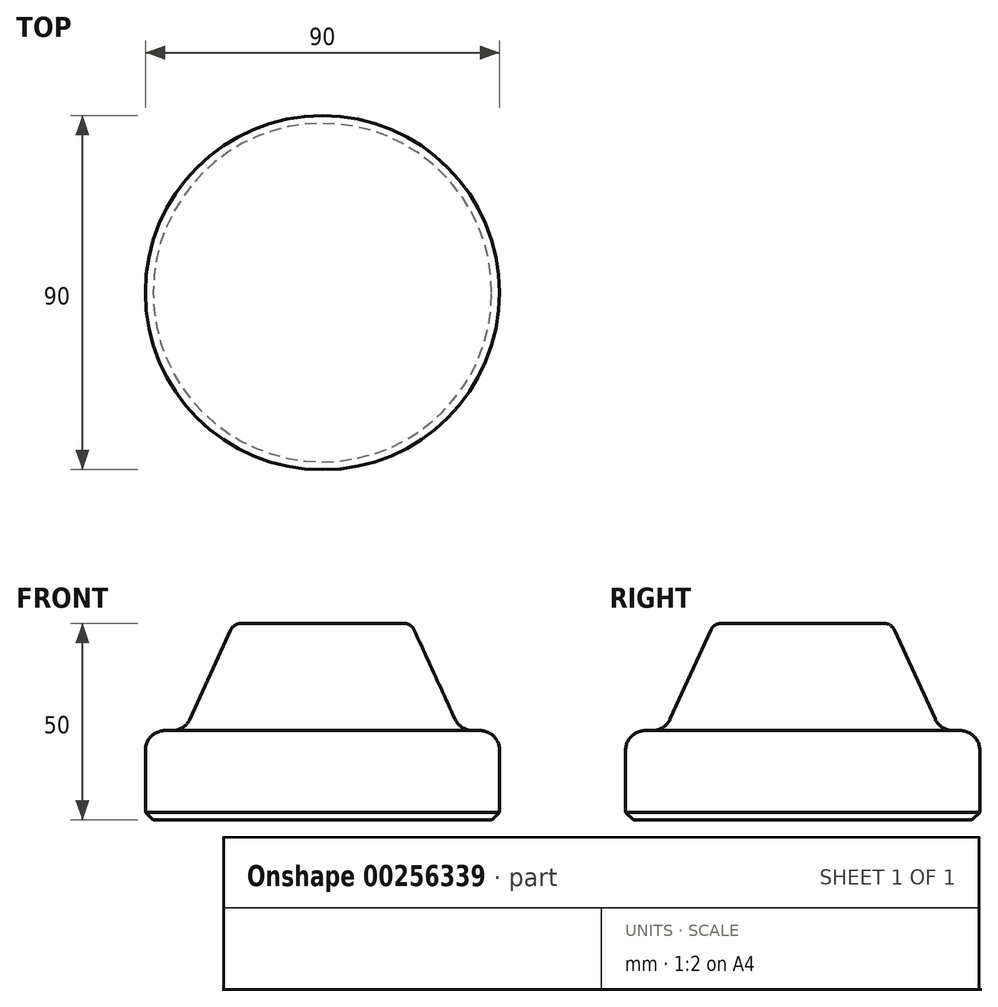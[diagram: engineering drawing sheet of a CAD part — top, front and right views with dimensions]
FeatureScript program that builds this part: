
annotation { "Feature Type Name" : "Feature", "Feature Type Description" : "" }
export const myFeature = defineFeature(function(context is Context, id is Id, definition is map)
    precondition{}
    {
        {
            var Q0;
            Q0=qCreatedBy(makeId("Front.planeOp"),FACE);
            var sketch = newSketch(context, id + "F0", { "sketchPlane" : qUnion([Q0])});
            skLineSegment(sketch, "E0", {"start": v(0, 50) * mm, "end": v(0, 0) * mm});
            skLineSegment(sketch, "E1", {"start": v(0, 0) * mm, "end": v(45, 0) * mm});
            skLineSegment(sketch, "E2", {"start": v(45, 0) * mm, "end": v(45, 17.73) * mm});
            skLineSegment(sketch, "E3", {"start": v(40, 22.73) * mm, "end": v(38.2, 22.73) * mm});
            skLineSegment(sketch, "E4", {"start": v(33.66, 25.64) * mm, "end": v(23.3, 48.25) * mm});
            skLineSegment(sketch, "E5", {"start": v(20.57, 50) * mm, "end": v(0, 50) * mm});
            skPoint(sketch, "E6.visualSharp", {"position": v(22.5, 50) * mm});
            skArc(sketch, "E6.filletArc", {"start": v(23.3, 48.25) * mm, "mid": v(22.2, 49.52) * mm, "end": v(20.57, 50) * mm});
            skPoint(sketch, "E7.visualSharp", {"position": v(35, 22.73) * mm});
            skArc(sketch, "E7.filletArc", {"start": v(33.66, 25.64) * mm, "mid": v(35.5, 23.52) * mm, "end": v(38.2, 22.73) * mm});
            skPoint(sketch, "E8.visualSharp", {"position": v(45, 22.73) * mm});
            skArc(sketch, "E8.filletArc", {"start": v(45, 17.73) * mm, "mid": v(43.54, 21.26) * mm, "end": v(40, 22.73) * mm});
            skLineSegment(sketch, "E9", {"start": v(0, 68.7) * mm, "end": v(0, -45.47) * mm});
            skSolve(sketch);
        }
        {
            var Q0;
            {var subQ1=sQuery(id+"F0.wireOp",EDGE,"E1");Q0=makeQuery(id+"F0.imprint","IMPRINT",FACE,{"disambiguationData":[TD([[makeQuery(id+"F0.imprint","IMPRINT",EDGE,{"derivedFrom":subQ1}),1.0]])]});}
            var Q1;
            Q1=sQuery(id+"F0.wireOp",EDGE,"E9");
            revolve(context, id + "F1", {"entities" : qUnion([Q0]), "axis" : qUnion([Q1]), "revolveType" : RevolveType.FULL});
        }
        {
            var Q0;
            Q0=makeQuery(id+"F1.opRevolve","SWEPT_EDGE",EDGE,{"disambiguationData":[OSD([sQuery(id+"F0.wireOp",EDGE,"E1"),sQuery(id+"F0.wireOp",EDGE,"E2")])]});
            chamfer(context, id + "F2", {"entities" : qUnion([Q0]), "width" : 2 * mm, "tangentPropagation" : true});
        }
    });
